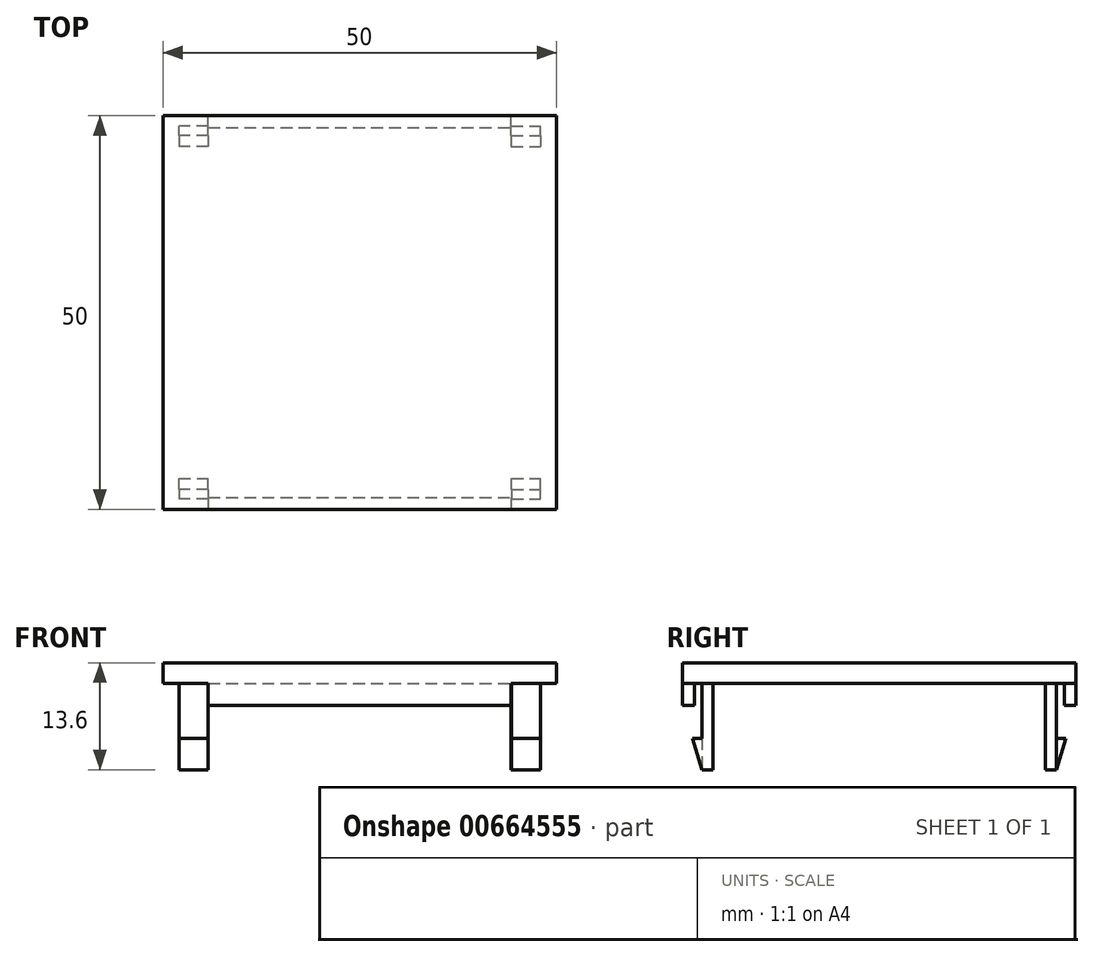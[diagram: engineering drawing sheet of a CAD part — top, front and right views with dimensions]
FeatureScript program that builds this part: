
annotation { "Feature Type Name" : "Feature", "Feature Type Description" : "" }
export const myFeature = defineFeature(function(context is Context, id is Id, definition is map)
    precondition{}
    {
        {
            var Q0;
            Q0=qCreatedBy(makeId("Top.planeOp"),FACE);
            var sketch = newSketch(context, id + "F0", { "sketchPlane" : qUnion([Q0])});
            skLineSegment(sketch, "E0.bottom", {"start": v(-25, 25) * mm, "end": v(25, 25) * mm});
            skLineSegment(sketch, "E0.top", {"start": v(-25, -25) * mm, "end": v(25, -25) * mm});
            skLineSegment(sketch, "E0.left", {"start": v(-25, 25) * mm, "end": v(-25, -25) * mm});
            skLineSegment(sketch, "E0.right", {"start": v(25, 25) * mm, "end": v(25, -25) * mm});
            skSolve(sketch);
        }
        {
            var Q0;
            Q0 = qSketchRegion(id + "F0", true);
            extrude(context, id + "F1", {"entities" : qUnion([Q0]), "depth" : 2.6 * mm, "offsetDistance" : 25 * mm});
        }
        {
            var Q0;
            Q0=makeQuery(id+"F1.opExtrude","CAP_FACE",FACE,{"disambiguationData":[OSD([sQuery(id+"F0.wireOp",EDGE,"E0.bottom"),sQuery(id+"F0.wireOp",EDGE,"E0.top"),sQuery(id+"F0.wireOp",EDGE,"E0.left"),sQuery(id+"F0.wireOp",EDGE,"E0.right")])],"isStart":true});
            cPlane(context, id + "F2", {"entities" : qUnion([Q0]), "cplaneType" : CPlaneType.OFFSET, "offset" : 0 * mm, "width" : 150 * mm, "height" : 150 * mm});
        }
        {
            var Q0;
            Q0=qCreatedBy(id+"F2.planeOp",FACE);
            var sketch = newSketch(context, id + "F3", { "sketchPlane" : qUnion([Q0])});
            skLineSegment(sketch, "E1.bottom", {"start": v(-19.25, 23.5) * mm, "end": v(19.25, 23.5) * mm});
            skLineSegment(sketch, "E1.top", {"start": v(-19.25, 25) * mm, "end": v(19.25, 25) * mm});
            skLineSegment(sketch, "E1.left", {"start": v(-19.25, 23.5) * mm, "end": v(-19.25, 25) * mm});
            skLineSegment(sketch, "E1.right", {"start": v(19.25, 23.5) * mm, "end": v(19.25, 25) * mm});
            skLineSegment(sketch, "E2.bottom", {"start": v(-19.25, -23.5) * mm, "end": v(19.25, -23.5) * mm});
            skLineSegment(sketch, "E2.top", {"start": v(-19.25, -25) * mm, "end": v(19.25, -25) * mm});
            skLineSegment(sketch, "E2.left", {"start": v(-19.25, -23.5) * mm, "end": v(-19.25, -25) * mm});
            skLineSegment(sketch, "E2.right", {"start": v(19.25, -23.5) * mm, "end": v(19.25, -25) * mm});
            skSolve(sketch);
        }
        {
            var Q0;
            Q0 = qSketchRegion(id + "F3", true);
            extrude(context, id + "F4", {"entities" : qUnion([Q0]), "operationType" : NewBodyOperationType.ADD, "depth" : 2.8 * mm, "offsetDistance" : 25 * mm});
        }
        {
            var Q0;
            Q0=qCreatedBy(id+"F2.planeOp",FACE);
            var sketch = newSketch(context, id + "F5", { "sketchPlane" : qUnion([Q0])});
            skLineSegment(sketch, "E3.bottom", {"start": v(19.29, 22.5) * mm, "end": v(22.99, 22.5) * mm});
            skLineSegment(sketch, "E3.top", {"start": v(19.29, 21.1) * mm, "end": v(22.99, 21.1) * mm});
            skLineSegment(sketch, "E3.left", {"start": v(19.29, 22.5) * mm, "end": v(19.29, 21.1) * mm});
            skLineSegment(sketch, "E3.right", {"start": v(22.99, 22.5) * mm, "end": v(22.99, 21.1) * mm});
            skLineSegment(sketch, "E4.bottom", {"start": v(-22.95, 22.5) * mm, "end": v(-19.25, 22.5) * mm});
            skLineSegment(sketch, "E4.top", {"start": v(-22.95, 21.1) * mm, "end": v(-19.25, 21.1) * mm});
            skLineSegment(sketch, "E4.left", {"start": v(-22.95, 22.5) * mm, "end": v(-22.95, 21.1) * mm});
            skLineSegment(sketch, "E4.right", {"start": v(-19.25, 22.5) * mm, "end": v(-19.25, 21.1) * mm});
            skLineSegment(sketch, "E5.bottom", {"start": v(-19.25, -22.5) * mm, "end": v(-22.95, -22.5) * mm});
            skLineSegment(sketch, "E5.top", {"start": v(-19.25, -21.1) * mm, "end": v(-22.95, -21.1) * mm});
            skLineSegment(sketch, "E5.left", {"start": v(-19.25, -22.5) * mm, "end": v(-19.25, -21.1) * mm});
            skLineSegment(sketch, "E5.right", {"start": v(-22.95, -22.5) * mm, "end": v(-22.95, -21.1) * mm});
            skLineSegment(sketch, "E6.bottom", {"start": v(19.25, -22.5) * mm, "end": v(22.95, -22.5) * mm});
            skLineSegment(sketch, "E6.top", {"start": v(19.25, -21.1) * mm, "end": v(22.95, -21.1) * mm});
            skLineSegment(sketch, "E6.left", {"start": v(19.25, -22.5) * mm, "end": v(19.25, -21.1) * mm});
            skLineSegment(sketch, "E6.right", {"start": v(22.95, -22.5) * mm, "end": v(22.95, -21.1) * mm});
            skSolve(sketch);
        }
        {
            var Q0;
            Q0 = qSketchRegion(id + "F5", true);
            extrude(context, id + "F6", {"entities" : qUnion([Q0]), "operationType" : NewBodyOperationType.ADD, "depth" : 11 * mm, "offsetDistance" : 25 * mm});
        }
        {
            var Q0;
            Q0=makeQuery(id+"F6.opExtrude","SWEPT_FACE",FACE,{"disambiguationData":[OSD([sQuery(id+"F5.wireOp",EDGE,"E3.right")])]});
            cPlane(context, id + "F7", {"entities" : qUnion([Q0]), "cplaneType" : CPlaneType.OFFSET, "offset" : 0 * mm, "width" : 150 * mm, "height" : 150 * mm});
        }
        {
            var Q0;
            Q0=qCreatedBy(id+"F7.planeOp",FACE);
            var sketch = newSketch(context, id + "F8", { "sketchPlane" : qUnion([Q0])});
            skLineSegment(sketch, "E7", {"start": v(-22.5, -11) * mm, "end": v(-23.7, -7) * mm});
            skLineSegment(sketch, "E8", {"start": v(-23.7, -7) * mm, "end": v(-22.5, -7) * mm});
            skLineSegment(sketch, "E9", {"start": v(-22.5, -7) * mm, "end": v(-22.5, -11) * mm});
            skSolve(sketch);
        }
        {
            var Q0;
            Q0 = qSketchRegion(id + "F8", true);
            extrude(context, id + "F9", {"entities" : qUnion([Q0]), "operationType" : NewBodyOperationType.ADD, "oppositeDirection" : true, "depth" : 3.7 * mm, "offsetDistance" : 25 * mm});
        }
        {
            var Q0;
            Q0=makeQuery(id+"F6.opExtrude","SWEPT_FACE",FACE,{"disambiguationData":[OSD([sQuery(id+"F5.wireOp",EDGE,"E4.left")])]});
            cPlane(context, id + "F10", {"entities" : qUnion([Q0]), "cplaneType" : CPlaneType.OFFSET, "offset" : 0 * mm, "width" : 150 * mm, "height" : 150 * mm});
        }
        {
            var Q0;
            Q0=qCreatedBy(id+"F10.planeOp",FACE);
            var sketch = newSketch(context, id + "F11", { "sketchPlane" : qUnion([Q0])});
            skLineSegment(sketch, "E10", {"start": v(22.5, -11) * mm, "end": v(23.7, -7) * mm});
            skLineSegment(sketch, "E11", {"start": v(23.7, -7) * mm, "end": v(22.5, -7) * mm});
            skLineSegment(sketch, "E12", {"start": v(22.5, -7) * mm, "end": v(22.5, -11) * mm});
            skSolve(sketch);
        }
        {
            var Q0;
            Q0 = qSketchRegion(id + "F11", true);
            extrude(context, id + "F12", {"entities" : qUnion([Q0]), "oppositeDirection" : true, "depth" : 3.7 * mm, "offsetDistance" : 25 * mm});
        }
        {
            var Q0;
            Q0=makeQuery(id+"F6.opExtrude","SWEPT_FACE",FACE,{"disambiguationData":[OSD([sQuery(id+"F5.wireOp",EDGE,"E5.right")])]});
            cPlane(context, id + "F13", {"entities" : qUnion([Q0]), "cplaneType" : CPlaneType.OFFSET, "offset" : 0 * mm, "width" : 150 * mm, "height" : 150 * mm});
        }
        {
            var Q0;
            Q0=qCreatedBy(id+"F13.planeOp",FACE);
            var sketch = newSketch(context, id + "F14", { "sketchPlane" : qUnion([Q0])});
            skLineSegment(sketch, "E13", {"start": v(-22.5, -11) * mm, "end": v(-23.7, -7) * mm});
            skLineSegment(sketch, "E14", {"start": v(-23.7, -7) * mm, "end": v(-22.5, -7) * mm});
            skLineSegment(sketch, "E15", {"start": v(-22.5, -7) * mm, "end": v(-22.5, -11) * mm});
            skSolve(sketch);
        }
        {
            var Q0;
            Q0 = qSketchRegion(id + "F14", true);
            extrude(context, id + "F15", {"entities" : qUnion([Q0]), "oppositeDirection" : true, "depth" : 3.7 * mm, "offsetDistance" : 25 * mm});
        }
        {
            var Q0;
            Q0=makeQuery(id+"F6.opExtrude","SWEPT_FACE",FACE,{"disambiguationData":[OSD([sQuery(id+"F5.wireOp",EDGE,"E6.right")])]});
            cPlane(context, id + "F16", {"entities" : qUnion([Q0]), "cplaneType" : CPlaneType.OFFSET, "offset" : 0 * mm, "width" : 150 * mm, "height" : 150 * mm});
        }
        {
            var Q0;
            Q0=qCreatedBy(id+"F16.planeOp",FACE);
            var sketch = newSketch(context, id + "F17", { "sketchPlane" : qUnion([Q0])});
            skLineSegment(sketch, "E16", {"start": v(22.5, -11) * mm, "end": v(23.7, -7) * mm});
            skLineSegment(sketch, "E17", {"start": v(23.7, -7) * mm, "end": v(22.5, -7) * mm});
            skLineSegment(sketch, "E18", {"start": v(22.5, -7) * mm, "end": v(22.5, -11) * mm});
            skSolve(sketch);
        }
        {
            var Q0;
            Q0 = qSketchRegion(id + "F17", true);
            extrude(context, id + "F18", {"entities" : qUnion([Q0]), "oppositeDirection" : true, "depth" : 3.7 * mm, "offsetDistance" : 25 * mm});
        }
    });
